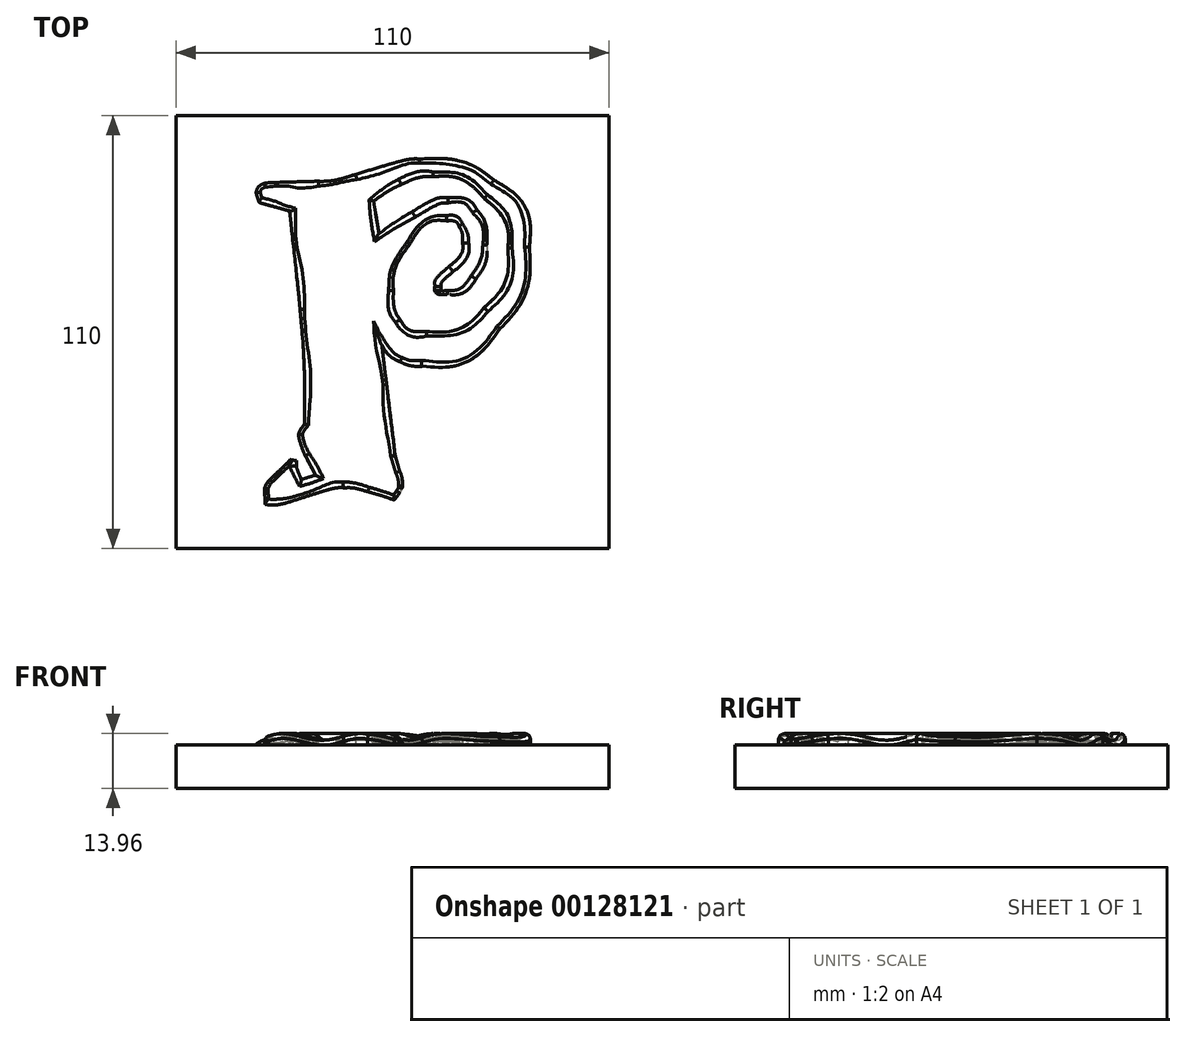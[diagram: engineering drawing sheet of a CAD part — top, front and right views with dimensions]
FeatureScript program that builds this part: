
annotation { "Feature Type Name" : "Feature", "Feature Type Description" : "" }
export const myFeature = defineFeature(function(context is Context, id is Id, definition is map)
    precondition{}
    {
        {
            var Q0;
            Q0=qCreatedBy(makeId("Top.planeOp"),FACE);
            var sketch = newSketch(context, id + "F0", { "sketchPlane" : qUnion([Q0])});
            skLineSegment(sketch, "E0.bottom", {"start": v(55, 55) * mm, "end": v(-55, 55) * mm});
            skLineSegment(sketch, "E0.top", {"start": v(55, -55) * mm, "end": v(-55, -55) * mm});
            skLineSegment(sketch, "E0.left", {"start": v(55, 55) * mm, "end": v(55, -55) * mm});
            skLineSegment(sketch, "E0.right", {"start": v(-55, 55) * mm, "end": v(-55, -55) * mm});
            skPoint(sketch, "E0.middle", {"position": v(0, 0) * mm});
            skSolve(sketch);
        }
        {
            var Q0;
            Q0=makeQuery(id+"F0.imprint","IMPRINT",FACE,{"disambiguationData":[TD([[makeQuery(id+"F0.imprint","IMPRINT",EDGE,{"derivedFrom":sQuery(id+"F0.wireOp",EDGE,"E0.bottom")}),1.0]])]});
            extrude(context, id + "F1", {"entities" : qUnion([Q0]), "oppositeDirection" : true, "depth" : 10 * mm});
        }
        {
            var Q0;
            Q0=qCreatedBy(makeId("Top.planeOp"),FACE);
            var sketch = newSketch(context, id + "F2", { "sketchPlane" : qUnion([Q0])});
            skFitSpline(sketch, "E1", {"points": [v(7.65, -8.7) * mm, v(5.5, -8.7) * mm, v(3.49, -8.28) * mm, v(1.61, -7.44) * mm]});
            skFitSpline(sketch, "E2", {"points": [v(1.61, -7.44) * mm, v(-0.16, -6.5) * mm, v(-1.61, -5.15) * mm, v(-2.74, -3.37) * mm]});
            skFitSpline(sketch, "E3", {"points": [v(-2.74, -3.37) * mm, v(-1.61, -12.73) * mm, v(-0.5, -22.04) * mm, v(0.63, -31.3) * mm]});
            skFitSpline(sketch, "E4", {"points": [v(0.63, -31.3) * mm, v(1, -32.62) * mm, v(1.38, -33.93) * mm, v(1.75, -35.24) * mm]});
            skFitSpline(sketch, "E5", {"points": [v(1.75, -35.24) * mm, v(2.22, -36.45) * mm, v(2.46, -37.72) * mm, v(2.46, -39.03) * mm]});
            skFitSpline(sketch, "E6", {"points": [v(2.46, -39.03) * mm, v(2.46, -39.5) * mm, v(2.22, -40.1) * mm, v(1.75, -40.85) * mm]});
            skFitSpline(sketch, "E7", {"points": [v(1.75, -40.85) * mm, v(1.29, -41.6) * mm, v(0.82, -42.21) * mm, v(0.35, -42.68) * mm]});
            skFitSpline(sketch, "E8", {"points": [v(0.35, -42.68) * mm, v(-1.8, -41.93) * mm, v(-4.05, -41.23) * mm, v(-6.39, -40.57) * mm]});
            skFitSpline(sketch, "E9", {"points": [v(-6.39, -40.57) * mm, v(-8.63, -39.92) * mm, v(-10.6, -39.6) * mm, v(-12.28, -39.6) * mm]});
            skFitSpline(sketch, "E10", {"points": [v(-12.28, -39.6) * mm, v(-14.06, -39.6) * mm, v(-18.04, -40.57) * mm, v(-24.22, -42.54) * mm]});
            skFitSpline(sketch, "E11", {"points": [v(-24.22, -42.54) * mm, v(-27.21, -43.47) * mm, v(-29.65, -43.94) * mm, v(-31.52, -43.94) * mm]});
            skFitSpline(sketch, "E12", {"points": [v(-32.5, -41.28) * mm, v(-32.5, -39.68) * mm, v(-31.7, -38.1) * mm, v(-30.11, -36.5) * mm]});
            skFitSpline(sketch, "E13", {"points": [v(-30.11, -36.5) * mm, v(-27.5, -33.97) * mm, v(-26.14, -32.62) * mm, v(-26.04, -32.43) * mm]});
            skLineSegment(sketch, "E14", {"start": v(-31.52, -43.94) * mm, "end": v(-32.36, -43.8) * mm});
            skLineSegment(sketch, "E15", {"start": v(-32.36, -43.8) * mm, "end": v(-32.5, -41.28) * mm});
            skFitSpline(sketch, "E16", {"points": [v(-19.58, -36.36) * mm, v(-20.43, -34.77) * mm, v(-21.27, -33.18) * mm, v(-22.11, -31.59) * mm]});
            skFitSpline(sketch, "E17", {"points": [v(-22.11, -31.59) * mm, v(-22.86, -29.9) * mm, v(-23.47, -28.13) * mm, v(-23.94, -26.25) * mm]});
            skFitSpline(sketch, "E18", {"points": [v(-23.94, -26.25) * mm, v(-23.66, -25.32) * mm, v(-23.14, -24.38) * mm, v(-22.4, -23.45) * mm]});
            skLineSegment(sketch, "E19", {"start": v(-26.04, -32.43) * mm, "end": v(-24.36, -32.71) * mm});
            skLineSegment(sketch, "E20", {"start": v(-24.36, -32.71) * mm, "end": v(-24.5, -34.26) * mm});
            skLineSegment(sketch, "E21", {"start": v(-24.5, -34.26) * mm, "end": v(-23.23, -37.48) * mm});
            skLineSegment(sketch, "E22", {"start": v(-23.23, -37.48) * mm, "end": v(-19.58, -36.36) * mm});
            skFitSpline(sketch, "E23", {"points": [v(-22.4, -19.65) * mm, v(-22.4, -11.51) * mm, v(-22.77, -3.09) * mm, v(-23.52, 5.62) * mm]});
            skFitSpline(sketch, "E24", {"points": [v(-23.52, 5.62) * mm, v(-23.7, 7.86) * mm, v(-24.6, 16.24) * mm, v(-26.18, 30.75) * mm]});
            skLineSegment(sketch, "E25", {"start": v(-22.4, -23.45) * mm, "end": v(-22.4, -19.65) * mm});
            skLineSegment(sketch, "E26", {"start": v(-22.4, -19.65) * mm, "end": v(-22.4, -23.45) * mm});
            skFitSpline(sketch, "E27", {"points": [v(-34.75, 35.24) * mm, v(-34.47, 36.45) * mm, v(-33.67, 37.34) * mm, v(-32.36, 37.9) * mm]});
            skLineSegment(sketch, "E28", {"start": v(-26.18, 30.75) * mm, "end": v(-33.9, 32.85) * mm});
            skLineSegment(sketch, "E29", {"start": v(-33.9, 32.85) * mm, "end": v(-34.75, 35.24) * mm});
            skFitSpline(sketch, "E30", {"points": [v(-18.88, 38.33) * mm, v(-16.36, 38.33) * mm, v(-13.22, 38.89) * mm, v(-9.48, 40.01) * mm]});
            skFitSpline(sketch, "E31", {"points": [v(-9.48, 40.01) * mm, v(-0.77, 42.63) * mm, v(4.75, 43.94) * mm, v(7.09, 43.94) * mm]});
            skFitSpline(sketch, "E32", {"points": [v(7.09, 43.94) * mm, v(14.4, 43.94) * mm, v(20.66, 42.12) * mm, v(25.9, 38.47) * mm]});
            skFitSpline(sketch, "E33", {"points": [v(25.9, 38.47) * mm, v(31.8, 34.35) * mm, v(34.75, 28.73) * mm, v(34.75, 21.62) * mm]});
            skFitSpline(sketch, "E34", {"points": [v(34.75, 21.62) * mm, v(34.75, 13.66) * mm, v(32.27, 6.74) * mm, v(27.3, 0.84) * mm]});
            skFitSpline(sketch, "E35", {"points": [v(27.3, 0.84) * mm, v(21.97, -5.52) * mm, v(15.42, -8.7) * mm, v(7.65, -8.7) * mm]});
            skLineSegment(sketch, "E36", {"start": v(-32.36, 37.9) * mm, "end": v(-18.88, 38.33) * mm});
            skLineSegment(sketch, "E37", {"start": v(-18.88, 38.33) * mm, "end": v(-32.36, 37.9) * mm});
            skFitSpline(sketch, "E38", {"points": [v(10.32, 39.45) * mm, v(7.89, 39.45) * mm, v(5.22, 38.8) * mm, v(2.32, 37.48) * mm]});
            skFitSpline(sketch, "E39", {"points": [v(2.32, 37.48) * mm, v(0.44, 36.64) * mm, v(-1.94, 35.24) * mm, v(-4.84, 33.27) * mm]});
            skFitSpline(sketch, "E40", {"points": [v(-3.44, 24.99) * mm, v(-0.63, 27.05) * mm, v(2.13, 28.87) * mm, v(4.84, 30.46) * mm]});
            skFitSpline(sketch, "E41", {"points": [v(4.84, 30.46) * mm, v(8.96, 32.9) * mm, v(12, 34.12) * mm, v(13.97, 34.12) * mm]});
            skFitSpline(sketch, "E42", {"points": [v(13.97, 34.12) * mm, v(17.43, 34.12) * mm, v(19.96, 33.04) * mm, v(21.55, 30.89) * mm]});
            skFitSpline(sketch, "E43", {"points": [v(21.55, 30.89) * mm, v(23.14, 28.73) * mm, v(23.94, 25.83) * mm, v(23.94, 22.18) * mm]});
            skFitSpline(sketch, "E44", {"points": [v(23.94, 22.18) * mm, v(23.94, 19.1) * mm, v(23, 16.2) * mm, v(21.13, 13.48) * mm]});
            skFitSpline(sketch, "E45", {"points": [v(21.13, 13.48) * mm, v(19.26, 10.86) * mm, v(16.78, 9.55) * mm, v(13.69, 9.55) * mm]});
            skFitSpline(sketch, "E46", {"points": [v(13.69, 9.55) * mm, v(11.72, 9.55) * mm, v(10.74, 10.3) * mm, v(10.74, 11.8) * mm]});
            skFitSpline(sketch, "E47", {"points": [v(10.74, 11.8) * mm, v(10.74, 12.92) * mm, v(11.9, 14.5) * mm, v(14.25, 16.57) * mm]});
            skFitSpline(sketch, "E48", {"points": [v(14.25, 16.57) * mm, v(16.59, 18.63) * mm, v(17.76, 20.68) * mm, v(17.76, 22.74) * mm]});
            skFitSpline(sketch, "E49", {"points": [v(17.76, 22.74) * mm, v(17.76, 24.43) * mm, v(17.48, 25.74) * mm, v(16.92, 26.67) * mm]});
            skFitSpline(sketch, "E50", {"points": [v(16.92, 26.67) * mm, v(16.45, 27.7) * mm, v(15.42, 28.22) * mm, v(13.83, 28.22) * mm]});
            skFitSpline(sketch, "E51", {"points": [v(13.83, 28.22) * mm, v(10.18, 28.22) * mm, v(7, 26.2) * mm, v(4.28, 22.18) * mm]});
            skFitSpline(sketch, "E52", {"points": [v(4.28, 22.18) * mm, v(1.57, 18.25) * mm, v(0.21, 14.37) * mm, v(0.21, 10.53) * mm]});
            skFitSpline(sketch, "E53", {"points": [v(0.21, 10.53) * mm, v(0.21, 7.35) * mm, v(0.82, 4.82) * mm, v(2.04, 2.95) * mm]});
            skFitSpline(sketch, "E54", {"points": [v(2.04, 2.95) * mm, v(3.35, 1.08) * mm, v(5.55, 0.14) * mm, v(8.63, 0.14) * mm]});
            skFitSpline(sketch, "E55", {"points": [v(8.63, 0.14) * mm, v(14.44, 0.14) * mm, v(19.3, 2.15) * mm, v(23.23, 6.18) * mm]});
            skFitSpline(sketch, "E56", {"points": [v(23.23, 6.18) * mm, v(27.26, 10.3) * mm, v(29.27, 15.3) * mm, v(29.27, 21.2) * mm]});
            skFitSpline(sketch, "E57", {"points": [v(29.27, 21.2) * mm, v(29.27, 25.97) * mm, v(27.3, 30.18) * mm, v(23.38, 33.83) * mm]});
            skFitSpline(sketch, "E58", {"points": [v(23.38, 33.83) * mm, v(19.54, 37.58) * mm, v(15.19, 39.45) * mm, v(10.32, 39.45) * mm]});
            skLineSegment(sketch, "E59", {"start": v(-4.84, 33.27) * mm, "end": v(-3.44, 24.99) * mm});
            skLineSegment(sketch, "E60", {"start": v(-3.44, 24.99) * mm, "end": v(-4.84, 33.27) * mm});
            skSolve(sketch);
        }
        {
            var Q0;
            Q0=makeQuery(id+"F2.imprint","IMPRINT",FACE,{"disambiguationData":[TD([[makeQuery(id+"F2.imprint","IMPRINT",EDGE,{"derivedFrom":sQuery(id+"F2.wireOp",EDGE,"E1")}),-1.0]])]});
            extrude(context, id + "F3", {"entities" : qUnion([Q0]), "operationType" : NewBodyOperationType.ADD, "depth" : 4.1 * mm});
        }
        {
            var Q0;
            Q0=qCreatedBy(makeId("Top.planeOp"),FACE);
            var sketch = newSketch(context, id + "F4", { "sketchPlane" : qUnion([Q0])});
            skLineSegment(sketch, "E61", {"start": v(0, 0) * mm, "end": v(-69.7, 47.83) * mm});
            skSolve(sketch);
        }
        {
            var Q0;
            Q0=sQuery(id+"F4.wireOp",EDGE,"E61");
            var Q1;
            Q1=qCreatedBy(makeId("Right.planeOp"),FACE);
            cPlane(context, id + "F5", {"entities" : qUnion([Q0, Q1]), "cplaneType" : CPlaneType.LINE_ANGLE, "offset" : 25 * mm, "angle" : 0 * degree, "width" : 150 * mm, "height" : 150 * mm});
        }
        {
            var Q0;
            Q0=qCreatedBy(id+"F5.planeOp",FACE);
            var sketch = newSketch(context, id + "F6", { "sketchPlane" : qUnion([Q0])});
            skFitSpline(sketch, "E62", {"points": [v(-51.6, 1.7) * mm, v(-45.97, 2.34) * mm, v(-41.52, 3.94) * mm, v(-36.73, 1.97) * mm, v(-29.9, 3.9) * mm, v(-22.88, 2.16) * mm, v(-14.66, 3.91) * mm, v(-6.26, 2.16) * mm, v(1.04, 3.91) * mm, v(7.22, 2.25) * mm, v(14.61, 3.91) * mm, v(27.08, 1.6) * mm, v(28.28, 1.42) * mm], "startDerivative": vector(74.4, -3.57) * mm, "endDerivative": vector(22.76, -1.06) * mm});
            skLineSegment(sketch, "E63", {"start": v(-51.6, 1.7) * mm, "end": v(-51.6, 10.23) * mm});
            skLineSegment(sketch, "E64", {"start": v(-51.6, 10.23) * mm, "end": v(27.72, 8.6) * mm});
            skLineSegment(sketch, "E65", {"start": v(27.72, 8.6) * mm, "end": v(28.28, 1.42) * mm});
            skSolve(sketch);
        }
        {
            var Q0;
            Q0 = qSketchRegion(id + "F6", true);
            extrude(context, id + "F7", {"entities" : qUnion([Q0]), "operationType" : NewBodyOperationType.REMOVE, "endBound" : BoundingType.THROUGH_ALL, "oppositeDirection" : true, "depth" : 25 * mm, "hasSecondDirection" : true, "secondDirectionBound" : SecondDirectionBoundingType.THROUGH_ALL, "secondDirectionOppositeDirection" : false, "secondDirectionDepth" : 25 * mm});
        }
        {
            var Q0;
            Q0=makeQuery(id+"F7.boolean.opBoolean","COPY",FACE,{"derivedFrom":makeQuery(id+"F7.opExtrude","SWEPT_FACE",FACE,{"disambiguationData":[OSD([sQuery(id+"F6.wireOp",EDGE,"E62")])]})});
            fillet(context, id + "F8", {"entities" : qUnion([Q0]), "radius" : 1.25 * mm, "tangentPropagation" : true, "allowEdgeOverflow" : false});
        }
        {
            var Q0;
            Q0=makeQuery(id+"F0.imprint","IMPRINT",FACE,{"disambiguationData":[TD([[makeQuery(id+"F0.imprint","IMPRINT",EDGE,{"derivedFrom":sQuery(id+"F0.wireOp",EDGE,"E0.bottom")}),1.0]])]});
            extrude(context, id + "F9", {"entities" : qUnion([Q0]), "operationType" : NewBodyOperationType.ADD, "depth" : 1 * mm});
        }
    });
